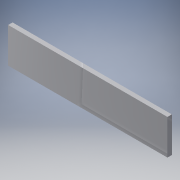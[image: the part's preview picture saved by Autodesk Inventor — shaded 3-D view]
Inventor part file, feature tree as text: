
AUTODESK INVENTOR PART (.ipt)
format: ipt  version: 2016 (Build 200138000, 138)  size: 89,088 bytes
history: native  units: in
note: dims shown in document units (in); Inventor stores cm internally (conversion verified against a paired STEP export)
features: extrude x1, sketch x1
ambient origin geometry x8: Origin, YZ Plane, XZ Plane, XY Plane, X Axis, Y Axis, Z Axis, Center Point
bodies: Solid1 (feature_tree)
feature tree (2):
  extrude  "Extrusion1"  Depth=4.525in
  sketch  "Sketch1"  dims[d0=1.0in d1=4.525in d2=0.125in d3=0.0in]
